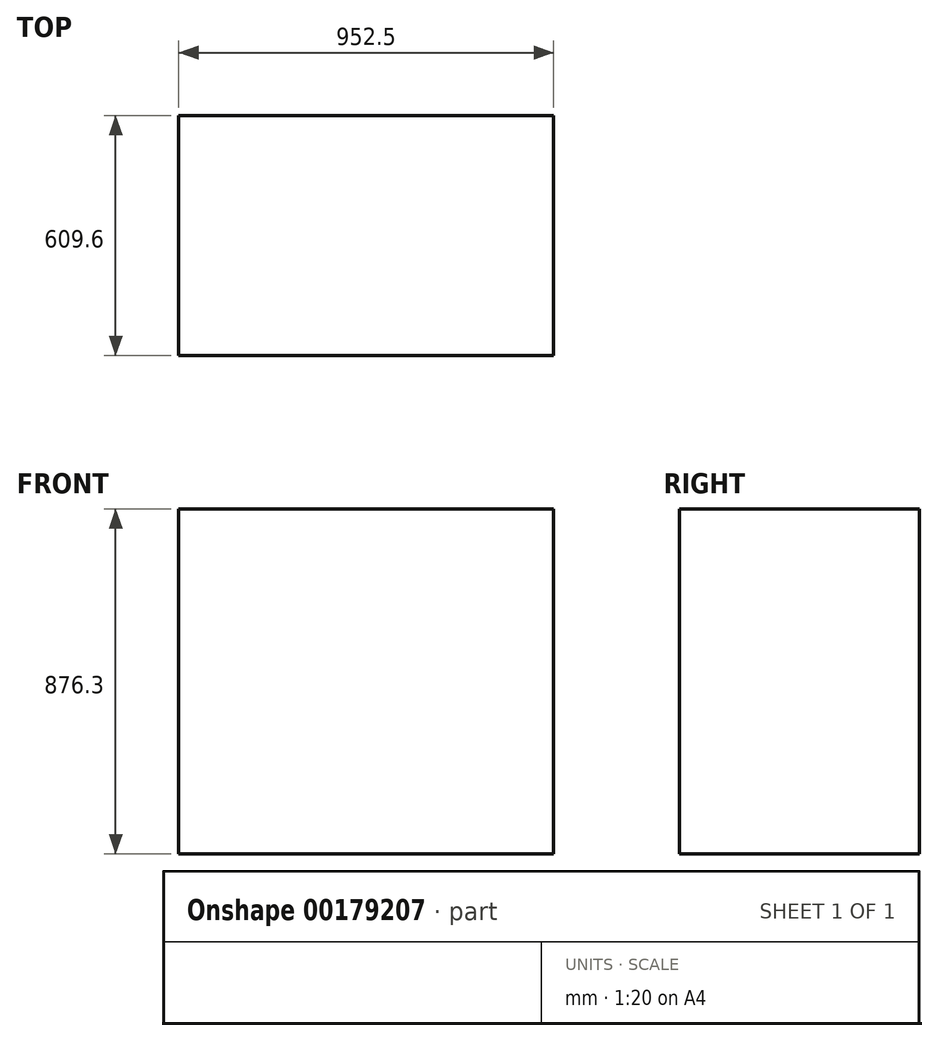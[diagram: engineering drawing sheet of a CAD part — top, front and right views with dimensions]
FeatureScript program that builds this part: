
annotation { "Feature Type Name" : "Feature", "Feature Type Description" : "" }
export const myFeature = defineFeature(function(context is Context, id is Id, definition is map)
    precondition{}
    {
        {
            var Q0;
            Q0=qCreatedBy(makeId("Top.planeOp"),FACE);
            var sketch = newSketch(context, id + "F0", { "sketchPlane" : qUnion([Q0])});
            skLineSegment(sketch, "E0.bottom", {"start": v(-476.25, 304.8) * mm, "end": v(476.25, 304.8) * mm});
            skLineSegment(sketch, "E0.top", {"start": v(-476.25, -304.8) * mm, "end": v(476.25, -304.8) * mm});
            skLineSegment(sketch, "E0.left", {"start": v(-476.25, 304.8) * mm, "end": v(-476.25, -304.8) * mm});
            skLineSegment(sketch, "E0.right", {"start": v(476.25, 304.8) * mm, "end": v(476.25, -304.8) * mm});
            skLineSegment(sketch, "E1", {"start": v(0, 304.8) * mm, "end": v(0, -304.8) * mm, "construction": true});
            skSolve(sketch);
        }
        {
            var Q0;
            Q0=makeQuery(id+"F0.imprint","IMPRINT",FACE,{"disambiguationData":[TD([[makeQuery(id+"F0.imprint","IMPRINT",EDGE,{"derivedFrom":sQuery(id+"F0.wireOp",EDGE,"E0.bottom")}),-1.0]])]});
            extrude(context, id + "F1", {"entities" : qUnion([Q0]), "depth" : 876.3 * mm});
        }
    });
